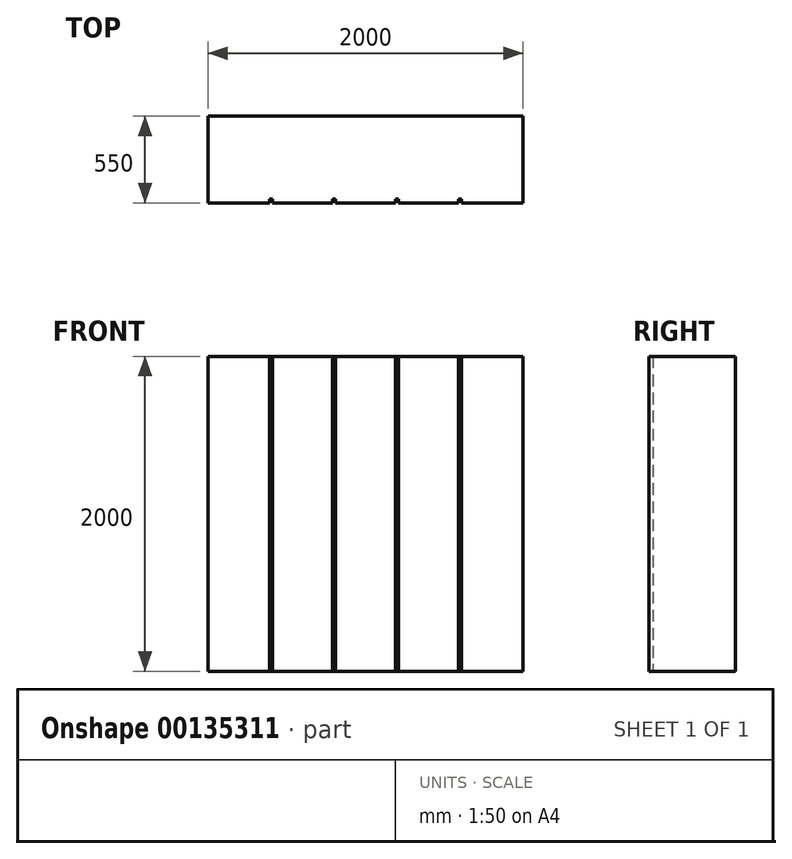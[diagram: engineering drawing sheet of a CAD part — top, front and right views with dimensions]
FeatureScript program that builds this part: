
annotation { "Feature Type Name" : "Feature", "Feature Type Description" : "" }
export const myFeature = defineFeature(function(context is Context, id is Id, definition is map)
    precondition{}
    {
        {
            var Q0;
            Q0=qCreatedBy(makeId("Top.planeOp"),FACE);
            var sketch = newSketch(context, id + "F0", { "sketchPlane" : qUnion([Q0])});
            skLineSegment(sketch, "E0.bottom", {"start": v(-1000, 275) * mm, "end": v(1000, 275) * mm});
            skLineSegment(sketch, "E0.top", {"start": v(-1000, -275) * mm, "end": v(1000, -275) * mm});
            skLineSegment(sketch, "E0.left", {"start": v(-1000, 275) * mm, "end": v(-1000, -275) * mm});
            skLineSegment(sketch, "E0.right", {"start": v(1000, 275) * mm, "end": v(1000, -275) * mm});
            skPoint(sketch, "E0.middle", {"position": v(0, 0) * mm});
            skSolve(sketch);
        }
        {
            var Q0;
            Q0 = qSketchRegion(id + "F0", true);
            extrude(context, id + "F1", {"entities" : qUnion([Q0]), "depth" : 2000 * mm});
        }
        {
            var Q0;
            Q0=makeQuery(id+"F1.opExtrude","SWEPT_FACE",FACE,{"disambiguationData":[OSD([sQuery(id+"F0.wireOp",EDGE,"E0.top")])]});
            var sketch = newSketch(context, id + "F2", { "sketchPlane" : qUnion([Q0])});
            skLineSegment(sketch, "E1.bottom", {"start": v(-610, 2000) * mm, "end": v(-590, 2000) * mm});
            skLineSegment(sketch, "E1.top", {"start": v(-610, 0) * mm, "end": v(-590, 0) * mm});
            skLineSegment(sketch, "E1.left", {"start": v(-610, 2000) * mm, "end": v(-610, 0) * mm});
            skLineSegment(sketch, "E1.right", {"start": v(-590, 2000) * mm, "end": v(-590, 0) * mm});
            skLineSegment(sketch, "E2", {"start": v(-600, 2000) * mm, "end": v(-600, 0) * mm, "construction": true});
            skLineSegment(sketch, "E3.1.0.0", {"start": v(-200, 2000) * mm, "end": v(-200, 0) * mm, "construction": true});
            skLineSegment(sketch, "E3.1.0.1", {"start": v(-190, 2000) * mm, "end": v(-190, 0) * mm});
            skLineSegment(sketch, "E3.1.0.2", {"start": v(-210, 2000) * mm, "end": v(-210, 0) * mm});
            skLineSegment(sketch, "E3.1.0.3", {"start": v(-210, 0) * mm, "end": v(-190, 0) * mm});
            skLineSegment(sketch, "E3.1.0.4", {"start": v(-210, 2000) * mm, "end": v(-190, 2000) * mm});
            skLineSegment(sketch, "E3.2.0.0", {"start": v(200, 2000) * mm, "end": v(200, 0) * mm, "construction": true});
            skLineSegment(sketch, "E3.2.0.1", {"start": v(210, 2000) * mm, "end": v(210, 0) * mm});
            skLineSegment(sketch, "E3.2.0.2", {"start": v(190, 2000) * mm, "end": v(190, 0) * mm});
            skLineSegment(sketch, "E3.2.0.3", {"start": v(190, 0) * mm, "end": v(210, 0) * mm});
            skLineSegment(sketch, "E3.2.0.4", {"start": v(190, 2000) * mm, "end": v(210, 2000) * mm});
            skLineSegment(sketch, "E3.3.0.0", {"start": v(600, 2000) * mm, "end": v(600, 0) * mm, "construction": true});
            skLineSegment(sketch, "E3.3.0.1", {"start": v(610, 2000) * mm, "end": v(610, 0) * mm});
            skLineSegment(sketch, "E3.3.0.2", {"start": v(590, 2000) * mm, "end": v(590, 0) * mm});
            skLineSegment(sketch, "E3.3.0.3", {"start": v(590, 0) * mm, "end": v(610, 0) * mm});
            skLineSegment(sketch, "E3.3.0.4", {"start": v(590, 2000) * mm, "end": v(610, 2000) * mm});
            skLineSegment(sketch, "E3.direction1", {"start": v(-610, 0) * mm, "end": v(-210, 0) * mm, "construction": true});
            skSolve(sketch);
        }
        {
            var Q0;
            Q0 = qSketchRegion(id + "F2", true);
            extrude(context, id + "F3", {"entities" : qUnion([Q0]), "operationType" : NewBodyOperationType.REMOVE, "oppositeDirection" : true, "depth" : 25 * mm});
        }
    });
